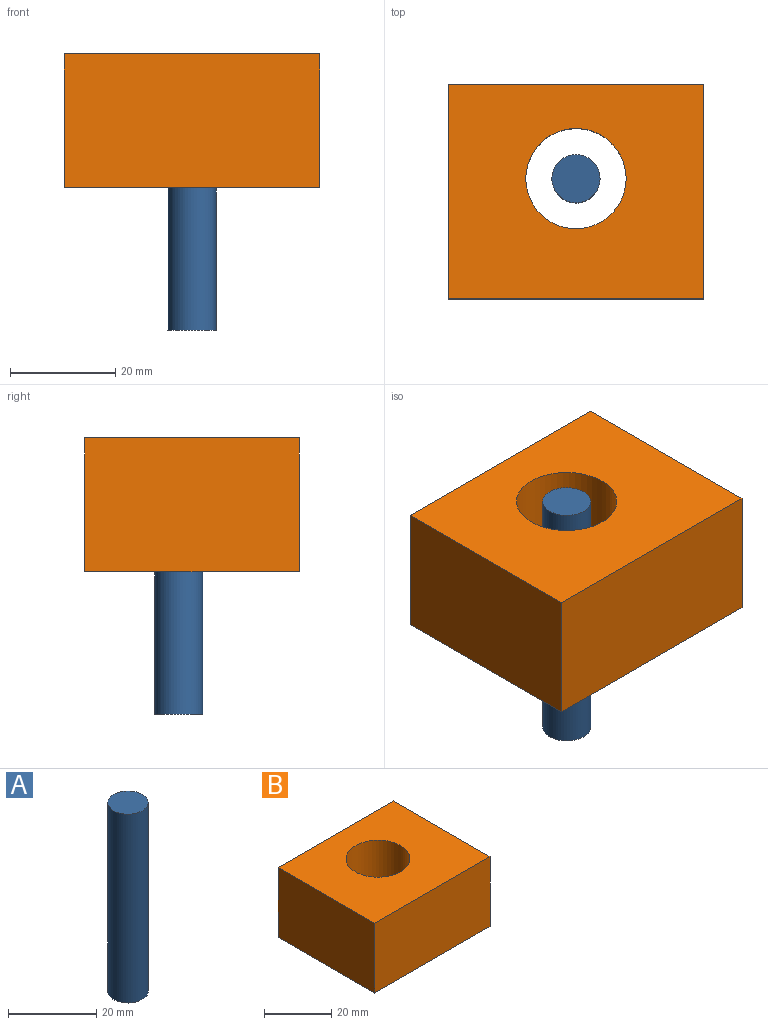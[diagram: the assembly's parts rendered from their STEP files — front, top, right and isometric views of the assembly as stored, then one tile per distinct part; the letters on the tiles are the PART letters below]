
ASSEMBLY  parts=2 mates=1
PART A: 3 faces, bbox 9.1x9.1x52.5 mm
  f0: cylinder r=4.57mm len=52.47mm, axis (0,0,-1), area 1506.2mm2, adj f1,f2
  f1: plane 9.14x9.14mm, normal (0,0,1), area 65.6mm2, adj f0
  f2: plane 9.14x9.14mm, normal (0,0,-1), area 65.6mm2, adj f0
PART B: 7 faces, bbox 48.5x40.7x25.4 mm
  f0: plane 48.55x25.4mm, normal (0,-1,0), area 1233mm2, adj f1,f3,f4,f5
  f1: plane 40.66x25.4mm, normal (1,0,0), area 1032.8mm2, adj f0,f2,f4,f5
  f2: plane 48.55x25.4mm, normal (0,1,0), area 1233mm2, adj f1,f3,f4,f5
  f3: plane 40.66x25.4mm, normal (-1,0,0), area 1032.8mm2, adj f0,f2,f4,f5
  f4: plane 48.55x40.66mm, normal (0,0,1), area 1688.9mm2, adj f0,f1,f2,f3,f6
  f5: plane 48.55x40.66mm, normal (0,0,-1), area 1688.9mm2, adj f0,f1,f2,f3,f6
  f6: cylinder r=9.53mm len=25.4mm, axis (0,0,1), area 1520.1mm2, adj f4,f5
PLACE A t=(13.11,25.27,-22.35)mm
PLACE B t=(13.11,2.42,4.72)mm
MATE revolute A.f0 <-> B.f6  axis (0,0,1) through (13.11,25.27,30.12)mm
